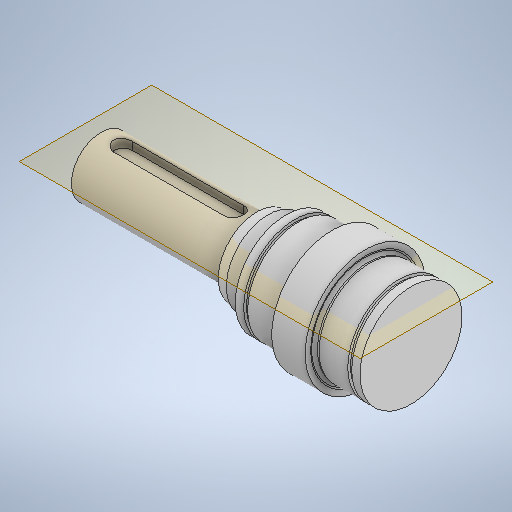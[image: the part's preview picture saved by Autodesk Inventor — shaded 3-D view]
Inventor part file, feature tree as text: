
AUTODESK INVENTOR PART (.ipt)
format: ipt  version: 2025.3 (Build 293356030, 356C)  size: 374,272 bytes
history: native  units: mm
features: sketch x8, revolve x7, plane x1, extrude x1, chamfer x1
ambient origin geometry x8: Origin, YZ Plane, XZ Plane, XY Plane, X Axis, Y Axis, Z Axis, Center Point
bodies: Body1 (feature_tree)
feature tree (18):
  revolve  "Umdrehung13"
  plane  "Arbeitsebene3"
  extrude  "Extrusion3"  Depth=16.0mm
  revolve  "Umdrehung14"
  chamfer  "Fasen1"  Distance=5.0mm
  revolve  "Umdrehung15"
  revolve  "Umdrehung16"
  revolve  "Umdrehung17"
  revolve  "Umdrehung18"
  revolve  "Umdrehung19"
  sketch  "Skizze15"  dims[d18=0.0mm d19=16.0mm d20=5.0mm d21=0.0mm]
  sketch  "Skizze16"  dims[d22=0.0mm]
  sketch  "Skizze17"  dims[d23=1.75mm d24=0.125mm d25=18.50049mm]
  sketch  "Skizze18"  dims[d26=0.0mm]
  sketch  "Skizze19"  dims[d27=0.0mm]
  sketch  "Skizze20"  dims[d28=0.0mm]
  sketch  "Skizze21"  dims[d29=0.0mm]
  sketch  "Skizze22"  dims[d30=0.0mm]
